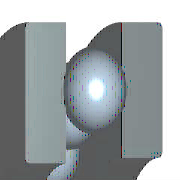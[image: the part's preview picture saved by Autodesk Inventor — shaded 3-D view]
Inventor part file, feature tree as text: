
AUTODESK INVENTOR PART (.ipt)
format: ipt  version: 2022 (Build 260153000, 153)  size: 323,072 bytes
history: native  units: mm (DEFAULTED — no unit token found)
features: sketch x1, other x1, pattern_circular x1
ambient origin geometry x8: Origin, YZ Plane, XZ Plane, XY Plane, X Axis, Y Axis, Z Axis, Center Point
bodies: Solid1 (feature_tree), Body (feature_tree)
feature tree (3):
  sketch  "Sketch"  dims[d0=2.2mm d9=90.0deg d10=90.0deg d1=130.0mm d2=360.0deg d3=4.84mm d4=0.6mm d5=0.6mm d6=0.0mm d7=0.0mm d8=30.0mm d11=32.0mm d12=39.5mm d13=47.0mm d14=47.0mm d15=5.5mm d16=11.0mm d18=3.3mm d19=0.0mm d46=0.0mm d47=0.0mm]
  other  "Ball"
  pattern_circular  "Balls"  Angle=90.0deg  [1 undecoded]
note: 1 required parameter value undecoded (feature->parameter linkage not recoverable at this tier; creation-order binding heuristic only, values carry confidence <= 0.55)
